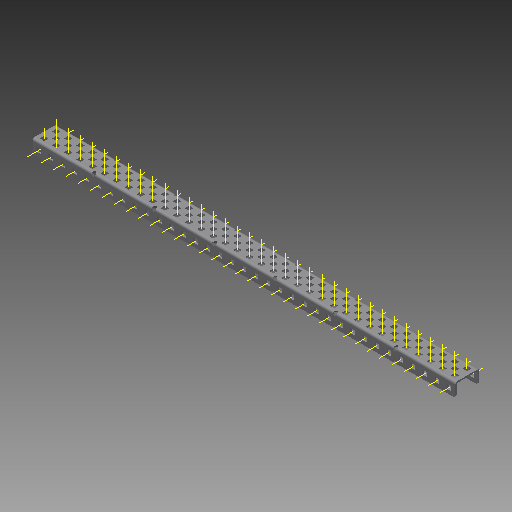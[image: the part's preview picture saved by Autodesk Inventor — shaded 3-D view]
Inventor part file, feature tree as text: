
AUTODESK INVENTOR PART (.ipt)
format: ipt  version: 2017 (Build 210142000, 142)  size: 2,299,904 bytes
history: native  units: in
note: dims shown in document units (in); Inventor stores cm internally (conversion verified against a paired STEP export)
features: other x181, pattern_linear x3, sheet_metal_op x1, extrude x1, imported_body x1, sketch x1
ambient origin geometry x8: Origin, YZ Plane, XZ Plane, XY Plane, X Axis, Y Axis, Z Axis, Center Point
bodies: Body1 (feature_tree)
feature tree (188):
  sheet_metal_op  "Fold1"
  other  "C-Channel"
  extrude  "length cut"  Depth=0.5in
  other  "top axis"
  other  "inner axis"
  other  "front axis"
  other  "back axis"
  pattern_linear  "top axes"  Spacing1=0.5in  [1 undecoded]
  pattern_linear  "inner axes"  Spacing1=0.5in  [1 undecoded]
  pattern_linear  "horiz axes"  Spacing1=-17.5in  [1 undecoded]
  other  "right plane"
  imported_body  "Base1"
  sketch  "Sketch1"  dims[d1=0.0in d4=0.5in d5=0.7874in d7=0.5in d10=0.5in d13=0.5in d14=-17.5in d15=0.0in d16=0.0in d17=0.0in d18=0.0in d19=0.0in]
  other  "Work Point1"
  other  "Work Point2"
  other  "Work Point3"
  other  "Work Point4"
  other  "Work Axis5"
  other  "Work Axis6"
  other  "Work Axis7"
  other  "Work Axis8"
  other  "Work Axis11"
  other  "Work Axis12"
  other  "Work Axis13"
  other  "Work Axis14"
  other  "Work Axis15"
  other  "Work Axis18"
  other  "Work Axis19"
  other  "Work Axis20"
  other  "Work Axis23"
  other  "Work Axis24"
  other  "Work Axis25"
  other  "Work Axis26"
  other  "Work Axis30"
  other  "Work Axis31"
  other  "Work Axis32"
  other  "Work Axis33"
  other  "left plane"
  other  "Work Axis37"
  other  "Work Axis38"
  other  "Work Axis39"
  other  "Work Axis40"
  other  "Work Axis41"
  other  "Work Axis42"
  other  "Work Axis43"
  other  "Work Axis44"
  other  "Work Axis45"
  other  "Work Axis46"
  other  "Work Axis47"
  other  "Work Axis48"
  other  "Work Axis49"
  other  "Work Axis50"
  other  "Work Axis51"
  other  "Work Axis52"
  other  "Work Axis53"
  other  "Work Axis54"
  other  "Work Axis55"
  other  "Work Axis56"
  other  "Work Axis57"
  other  "Work Axis58"
  other  "Work Axis59"
  other  "Work Axis60"
  other  "Work Axis61"
  other  "Work Axis62"
  other  "Work Axis63"
  other  "Work Axis64"
  other  "Work Axis65"
  other  "Work Axis66"
  other  "Work Axis67"
  other  "Work Axis68"
  other  "Work Axis69"
  other  "Work Axis70"
  other  "Work Axis71"
  other  "Work Axis72"
  other  "Work Axis73"
  other  "Work Axis74"
  other  "Work Axis75"
  other  "Work Axis76"
  other  "Work Axis77"
  other  "Work Axis78"
  other  "Work Axis79"
  other  "Work Axis80"
  other  "Work Axis81"
  other  "Work Axis82"
  other  "Work Axis83"
  other  "Work Axis84"
  other  "Work Axis85"
  other  "Work Axis86"
  other  "Work Axis87"
  other  "Work Axis88"
  other  "Work Axis89"
  other  "Work Axis90"
  other  "Work Axis91"
  other  "Work Axis92"
  other  "Work Axis93"
  other  "Work Axis94"
  other  "Work Axis95"
  other  "Work Axis96"
  other  "Work Axis97"
  other  "Work Axis98"
  other  "Work Axis99"
  other  "Work Axis100"
  other  "Work Axis101"
  other  "Work Axis102"
  other  "Work Axis103"
  other  "Work Axis104"
  other  "Work Axis105"
  other  "Work Axis106"
  other  "Work Axis107"
  other  "Work Axis108"
  other  "Work Axis109"
  other  "Work Axis110"
  other  "Work Axis111"
  other  "Work Axis112"
  other  "Work Axis113"
  other  "Work Axis114"
  other  "Work Axis115"
  other  "Work Axis116"
  other  "Work Axis117"
  other  "Work Axis118"
  other  "Work Axis119"
  other  "Work Axis120"
  other  "Work Axis121"
  other  "Work Axis122"
  other  "Work Axis123"
  other  "Work Axis124"
  other  "Work Axis125"
  other  "Work Axis126"
  other  "Work Axis127"
  other  "Work Axis128"
  other  "Work Axis129"
  other  "Work Axis130"
  other  "Work Axis131"
  other  "Work Axis132"
  other  "Work Axis133"
  other  "Work Axis134"
  other  "Work Axis135"
  other  "Work Axis136"
  other  "Work Axis137"
  other  "Work Axis138"
  other  "Work Axis139"
  other  "Work Axis140"
  other  "Work Axis141"
  other  "Work Axis142"
  other  "Work Axis143"
  other  "Work Axis144"
  other  "Work Axis145"
  other  "Work Axis146"
  other  "Work Axis147"
  other  "Work Axis148"
  other  "Work Axis149"
  other  "Work Axis150"
  other  "Work Axis151"
  other  "Work Axis152"
  other  "Work Axis153"
  other  "Work Axis154"
  other  "Work Axis155"
  other  "Work Axis156"
  other  "Work Axis157"
  other  "Work Axis158"
  other  "Work Axis159"
  other  "Work Axis160"
  other  "Work Axis161"
  other  "Work Axis162"
  other  "Work Axis163"
  other  "Work Axis164"
  other  "Work Axis165"
  other  "Work Axis166"
  other  "Work Axis167"
  other  "Work Axis168"
  other  "Work Axis169"
  other  "Work Axis170"
  other  "Work Axis171"
  other  "Work Axis172"
  other  "Work Axis173"
  other  "Work Axis174"
  other  "Work Axis175"
  other  "Work Axis176"
  other  "Work Axis177"
  other  "Work Axis178"
  other  "Work Axis179"
  other  "Work Axis180"
  other  "Work Axis181"
  other  "Work Axis182"
  other  "Work Axis183"
  other  "Work Axis184"
  other  "Work Axis185"
  other  "Work Axis186"
note: 3 required parameter values undecoded (feature->parameter linkage not recoverable at this tier; creation-order binding heuristic only, values carry confidence <= 0.55)
